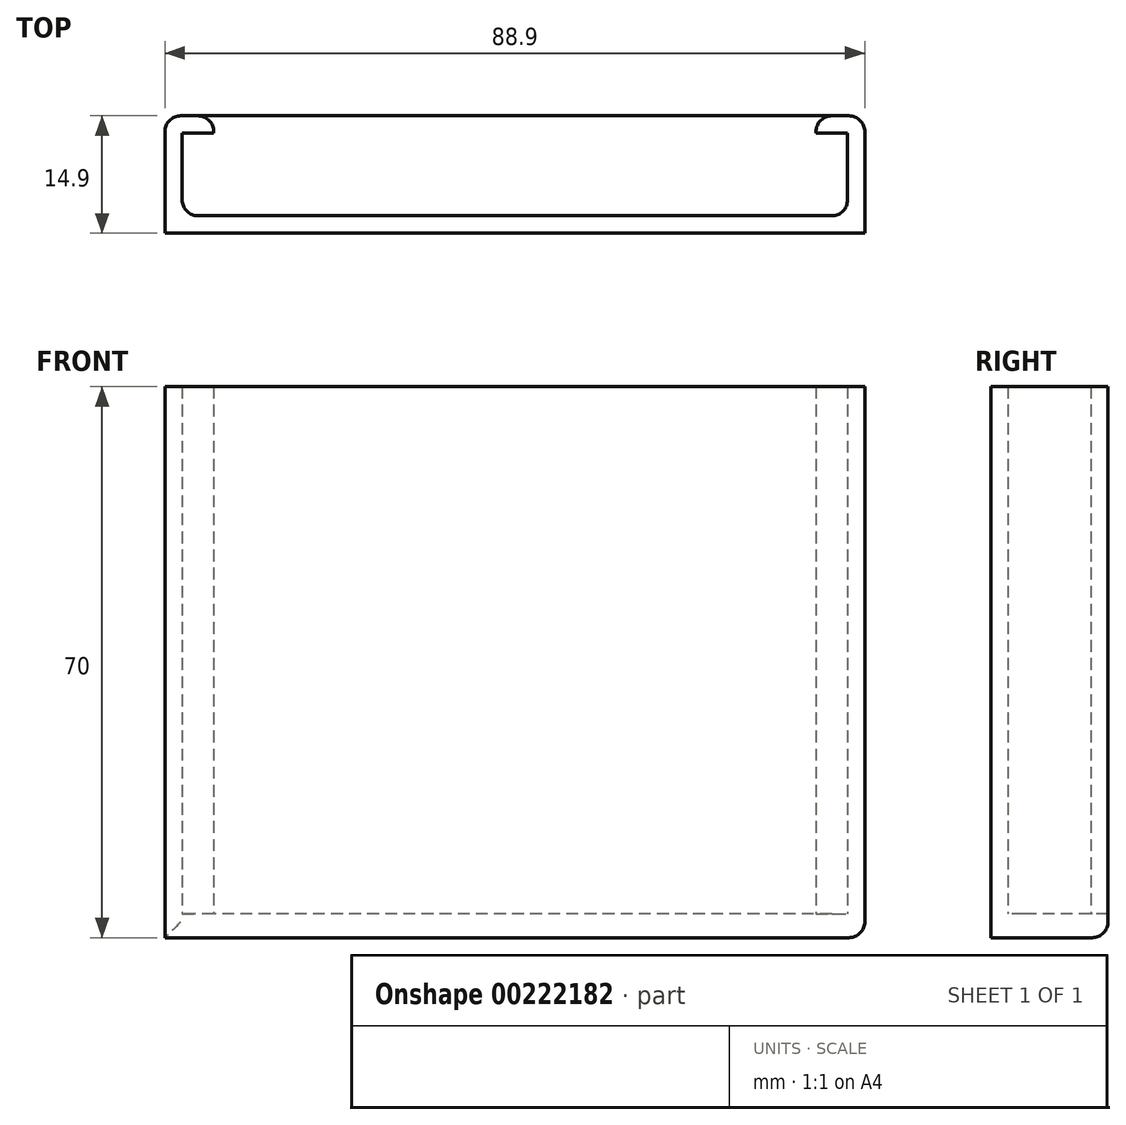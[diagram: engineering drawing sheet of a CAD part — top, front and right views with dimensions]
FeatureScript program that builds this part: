
annotation { "Feature Type Name" : "Feature", "Feature Type Description" : "" }
export const myFeature = defineFeature(function(context is Context, id is Id, definition is map)
    precondition{}
    {
        {
            var Q0;
            Q0=qCreatedBy(makeId("Top.planeOp"),FACE);
            var sketch = newSketch(context, id + "F0", { "sketchPlane" : qUnion([Q0])});
            skLineSegment(sketch, "E0", {"start": v(0, 7.22) * mm, "end": v(0, -7.47) * mm, "construction": true});
            skLineSegment(sketch, "E1", {"start": v(0, 0) * mm, "end": v(44.45, 0) * mm});
            skLineSegment(sketch, "E2", {"start": v(44.45, 0) * mm, "end": v(44.45, 14.9) * mm});
            skLineSegment(sketch, "E3", {"start": v(44.45, 14.9) * mm, "end": v(38.25, 14.9) * mm});
            skLineSegment(sketch, "E4", {"start": v(0, 2.2) * mm, "end": v(0, 0) * mm});
            skLineSegment(sketch, "E5.MirrorCS", {"start": v(-44.45, 0) * mm, "end": v(-44.45, 14.9) * mm});
            skLineSegment(sketch, "E6.MirrorCS", {"start": v(0, 0) * mm, "end": v(-44.45, 0) * mm});
            skLineSegment(sketch, "E7", {"start": v(38.25, 14.9) * mm, "end": v(38.25, 12.7) * mm});
            skLineSegment(sketch, "E8", {"start": v(38.25, 12.7) * mm, "end": v(42.25, 12.7) * mm});
            skLineSegment(sketch, "E9", {"start": v(42.25, 12.7) * mm, "end": v(42.25, 2.2) * mm});
            skLineSegment(sketch, "E10", {"start": v(42.25, 2.2) * mm, "end": v(0, 2.2) * mm});
            skLineSegment(sketch, "E11.MirrorCS", {"start": v(-42.25, 2.2) * mm, "end": v(0, 2.2) * mm});
            skLineSegment(sketch, "E12.MirrorCS", {"start": v(-42.25, 12.7) * mm, "end": v(-42.25, 2.2) * mm});
            skLineSegment(sketch, "E13.MirrorCS", {"start": v(-38.25, 12.7) * mm, "end": v(-42.25, 12.7) * mm});
            skLineSegment(sketch, "E14.MirrorCS", {"start": v(-38.25, 14.9) * mm, "end": v(-38.25, 12.7) * mm});
            skLineSegment(sketch, "E15.MirrorCS", {"start": v(-44.45, 14.9) * mm, "end": v(-38.25, 14.9) * mm});
            skLineSegment(sketch, "E16.top", {"start": v(-44.45, 0) * mm, "end": v(44.45, 0) * mm});
            skLineSegment(sketch, "E16.left", {"start": v(-44.45, 14.9) * mm, "end": v(-44.45, 0) * mm});
            skLineSegment(sketch, "E16.right", {"start": v(44.45, 14.6) * mm, "end": v(44.45, 0) * mm});
            skSolve(sketch);
        }
        {
            var Q0;
            Q0=makeQuery(id+"F0.imprint","IMPRINT",FACE,{"disambiguationData":[TD([[makeQuery(id+"F0.imprint","IMPRINT",EDGE,{"derivedFrom":sQuery(id+"F0.wireOp",EDGE,"E4")}),-1.0]])]});
            var Q1;
            Q1=makeQuery(id+"F0.imprint","IMPRINT",FACE,{"disambiguationData":[TD([[makeQuery(id+"F0.imprint","IMPRINT",EDGE,{"derivedFrom":sQuery(id+"F0.wireOp",EDGE,"E1")}),1.0]])]});
            var Q2;
            {var subQ1=sQuery(id+"F0.wireOp",EDGE,"E4");Q2=makeQuery(id+"F0.imprint","IMPRINT",FACE,{"disambiguationData":[TD([[makeQuery(id+"F0.imprint","IMPRINT",EDGE,{"derivedFrom":subQ1}),1.0]])]});}
            extrude(context, id + "F1", {"entities" : qUnion([Q0, Q1, Q2]), "depth" : 70 * mm});
        }
        {
            var Q0;
            {var subQ0=sQuery(id+"F0.wireOp",EDGE,"E4");Q0=makeQuery(id+"F0.imprint","IMPRINT",FACE,{"disambiguationData":[TD([[makeQuery(id+"F0.imprint","IMPRINT",EDGE,{"derivedFrom":subQ0}),-1.0]])]});}
            var sketch = newSketch(context, id + "F2", { "sketchPlane" : qUnion([Q0])});
            skLineSegment(sketch, "E17.bottom", {"start": v(44.45, 0) * mm, "end": v(-44.45, 0) * mm});
            skLineSegment(sketch, "E17.top", {"start": v(44.45, 14.9) * mm, "end": v(-44.45, 14.9) * mm});
            skLineSegment(sketch, "E17.left", {"start": v(44.45, 0) * mm, "end": v(44.45, 14.9) * mm});
            skLineSegment(sketch, "E17.right", {"start": v(-44.45, 0) * mm, "end": v(-44.45, 14.9) * mm});
            skSolve(sketch);
        }
        {
            var Q0;
            {var subQ1=sQuery(id+"F2.wireOp",EDGE,"E17.left");Q0=makeQuery(id+"F2.imprint","IMPRINT",FACE,{"disambiguationData":[TD([[makeQuery(id+"F2.imprint","IMPRINT",EDGE,{"derivedFrom":subQ1}),1.0]])]});}
            var Q1;
            {var subQ1=sQuery(id+"F2.wireOp",EDGE,"E17.right");Q1=makeQuery(id+"F2.imprint","IMPRINT",FACE,{"disambiguationData":[TD([[makeQuery(id+"F2.imprint","IMPRINT",EDGE,{"derivedFrom":subQ1}),1.0]])]});}
            extrude(context, id + "F3", {"entities" : qUnion([Q0, Q1]), "operationType" : NewBodyOperationType.ADD, "depth" : 3 * mm});
        }
        {
            var Q0;
            Q0=makeQuery(id+"F1.opExtrude","SWEPT_EDGE",EDGE,{"disambiguationData":[OSD([sQuery(id+"F0.wireOp",EDGE,"E16.top"),sQuery(id+"F0.wireOp",EDGE,"E16.right")])]});
            var Q1;
            Q1=makeQuery(id+"F1.opExtrude","SWEPT_EDGE",EDGE,{"disambiguationData":[OSD([sQuery(id+"F0.wireOp",EDGE,"E2"),sQuery(id+"F0.wireOp",EDGE,"E3")])]});
            var Q2;
            Q2=makeQuery(id+"F1.opExtrude","SWEPT_EDGE",EDGE,{"disambiguationData":[OSD([sQuery(id+"F0.wireOp",EDGE,"E3"),sQuery(id+"F0.wireOp",EDGE,"E7")])]});
            var Q3;
            Q3=makeQuery(id+"F1.opExtrude","SWEPT_EDGE",EDGE,{"disambiguationData":[OSD([sQuery(id+"F0.wireOp",EDGE,"E9"),sQuery(id+"F0.wireOp",EDGE,"E10")])]});
            var Q4;
            Q4=makeQuery(id+"F1.opExtrude","SWEPT_EDGE",EDGE,{"disambiguationData":[OSD([sQuery(id+"F0.wireOp",EDGE,"E14.MirrorCS"),sQuery(id+"F0.wireOp",EDGE,"E15.MirrorCS")])]});
            var Q5;
            Q5=makeQuery(id+"F1.opExtrude","SWEPT_EDGE",EDGE,{"disambiguationData":[OSD([sQuery(id+"F0.wireOp",EDGE,"E11.MirrorCS"),sQuery(id+"F0.wireOp",EDGE,"E12.MirrorCS")])]});
            var Q6;
            Q6=makeQuery(id+"F1.opExtrude","SWEPT_EDGE",EDGE,{"disambiguationData":[OSD([sQuery(id+"F0.wireOp",EDGE,"E15.MirrorCS"),sQuery(id+"F0.wireOp",EDGE,"E16.left")])]});
            var Q7;
            Q7=makeQuery(id+"F1.opExtrude","SWEPT_EDGE",EDGE,{"disambiguationData":[OSD([sQuery(id+"F0.wireOp",EDGE,"E16.top"),sQuery(id+"F0.wireOp",EDGE,"E16.left")])]});
            var Q8;
            Q8=makeQuery(id+"F1.opExtrude","CAP_EDGE",EDGE,{"disambiguationData":[OSD([sQuery(id+"F0.wireOp",EDGE,"E16.top")])],"isStart":true});
            var Q9;
            Q9=makeQuery(id+"F3.boolean.opBoolean","MERGE",EDGE,{"derivedFrom":[makeQuery(id+"F1.opExtrude","CAP_EDGE",EDGE,{"disambiguationData":[OSD([sQuery(id+"F0.wireOp",EDGE,"E3")])],"isStart":true}),makeQuery(id+"F1.opExtrude","CAP_EDGE",EDGE,{"disambiguationData":[OSD([sQuery(id+"F0.wireOp",EDGE,"E15.MirrorCS")])],"isStart":true}),makeQuery(id+"F3.opExtrude","CAP_EDGE",EDGE,{"disambiguationData":[OSD([sQuery(id+"F2.wireOp",EDGE,"E17.top")])],"isStart":true})]});
            var Q10;
            Q10=makeQuery(id+"F1.opExtrude","CAP_EDGE",EDGE,{"disambiguationData":[OSD([sQuery(id+"F0.wireOp",EDGE,"E16.left")])],"isStart":true});
            var Q11;
            Q11=makeQuery(id+"F1.opExtrude","CAP_EDGE",EDGE,{"disambiguationData":[OSD([sQuery(id+"F0.wireOp",EDGE,"E2"),sQuery(id+"F0.wireOp",EDGE,"E16.right")])],"isStart":true});
            fillet(context, id + "F4", {"entities" : qUnion([Q0, Q1, Q2, Q3, Q4, Q5, Q6, Q7, Q8, Q9, Q10, Q11]), "radius" : 2 * mm, "tangentPropagation" : true, "allowEdgeOverflow" : false});
        }
    });
